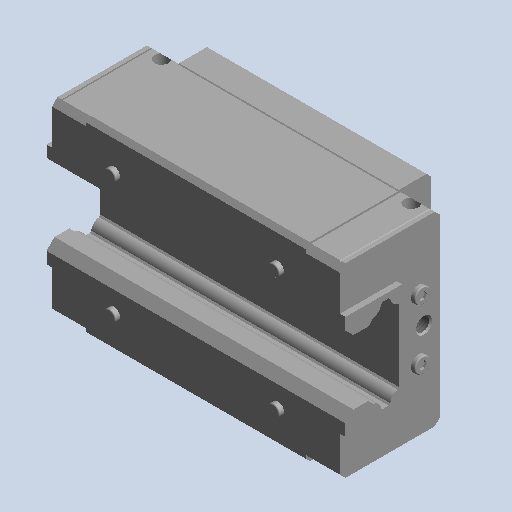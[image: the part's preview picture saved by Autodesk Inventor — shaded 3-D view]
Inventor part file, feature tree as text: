
AUTODESK INVENTOR PART (.ipt)
format: ipt  version: 2022 (Build 260153000, 153)  size: 424,960 bytes
history: native  units: mm (DEFAULTED — no unit token found)
features: sketch x39, extrude x22, other x21, revolve x10, hole x7, pattern_linear x1
ambient origin geometry x8: Origin, YZ Plane, XZ Plane, XY Plane, X Axis, Y Axis, Z Axis, Center Point
bodies: Solid1 (feature_tree)
feature tree (100):
  extrude  "Extrusion1"  Depth=2.0mm
  hole  "Hole1"  [1 undecoded]
  pattern_linear  "Rectangular Pattern1"  [2 undecoded]
  extrude  "Extrusion2"  [1 undecoded]
  extrude  "Extrusion3"  [1 undecoded]
  extrude  "Extrusion4"  [1 undecoded]
  extrude  "Extrusion5"  [1 undecoded]
  extrude  "Extrusion6"  [1 undecoded]
  extrude  "Extrusion7"  [1 undecoded]
  hole  "Hole2"  [1 undecoded]
  hole  "Hole3"  [1 undecoded]
  extrude  "Extrusion8"  [1 undecoded]
  extrude  "Extrusion9"  [1 undecoded]
  extrude  "Extrusion10"  [1 undecoded]
  extrude  "Extrusion11"  [1 undecoded]
  extrude  "Extrusion12"  [1 undecoded]
  revolve  "Revolution1"  [1 undecoded]
  revolve  "Revolution2"  [1 undecoded]
  revolve  "Revolution3"  [1 undecoded]
  revolve  "Revolution4"  [1 undecoded]
  extrude  "Extrusion13"  [1 undecoded]
  extrude  "Extrusion14"  [1 undecoded]
  extrude  "Extrusion15"  [1 undecoded]
  extrude  "Extrusion16"  [1 undecoded]
  extrude  "Extrusion17"  [1 undecoded]
  extrude  "Extrusion18"  [1 undecoded]
  extrude  "Extrusion19"  [1 undecoded]
  extrude  "Extrusion20"  [1 undecoded]
  extrude  "Extrusion21"  [1 undecoded]
  extrude  "Extrusion22"  [1 undecoded]
  hole  "Hole4"  [1 undecoded]
  hole  "Hole5"  [1 undecoded]
  revolve  "Revolution5"  [1 undecoded]
  revolve  "Revolution6"  [1 undecoded]
  revolve  "Revolution7"  [1 undecoded]
  revolve  "Revolution8"  [1 undecoded]
  revolve  "Revolution9"  [1 undecoded]
  hole  "Hole6"  [1 undecoded]
  revolve  "Revolution10"  [1 undecoded]
  hole  "Hole7"  [1 undecoded]
  other  "4TRACK_XY"
  other  "4TRACK_YZ"
  other  "4TRACK_ZX"
  other  "4TRACK_X"
  other  "4TRACK_Y"
  other  "4TRACK_Z"
  other  "4TRACK_Center"
  other  "niple_XY"
  other  "niple_YZ"
  other  "niple_ZX"
  other  "niple_X"
  other  "niple_Y"
  other  "niple_Z"
  other  "niple_Center"
  other  "niple2_XY"
  other  "niple2_YZ"
  other  "niple2_ZX"
  other  "niple2_X"
  other  "niple2_Y"
  other  "niple2_Z"
  other  "niple2_Center"
  sketch  "Sketch_22"  dims[d53=360.0deg]
  sketch  "Sketch2"  dims[d2=6.647mm d3=12.6765mm d4=8.0mm d5=2.0mm d6=90.0deg d7=14.4mm d8=120.0deg d9=20.0mm d11=50.0mm d12=20.0mm d14=50.0mm]
  sketch  "Sketch_7"  dims[d23=10.5mm d24=0.0mm]
  sketch  "Sketch_2"  dims[d15=11.0mm d16=0.0mm d17=3.5mm d18=0.0mm]
  sketch  "Sketch_8"  dims[d25=10.5mm d26=0.0mm]
  sketch  "Sketch_42"  dims[d82=4.917mm d83=5.5415mm d84=6.0mm d85=2.0mm d86=90.0deg d87=6.0mm d88=120.0deg]
  sketch  "Sketch_106"  dims[d102=5.2mm d103=6.0mm d104=4.0mm d105=2.0mm d106=90.0deg d107=5.2mm d108=0.0mm]
  sketch  "Sketch_107"  dims[d109=0.0mm d110=0.0mm]
  sketch  "Sketch9"  dims[d27=6.2mm d28=6.0mm d29=4.0mm d30=2.0mm d31=90.0deg d32=1.0mm d33=0.0mm]
  sketch  "Sketch10"  dims[d34=6.2mm d35=6.0mm d36=4.0mm d37=2.0mm d38=90.0deg d39=1.0mm d40=0.0mm]
  sketch  "Sketch_1"  dims[d0=80.4mm d1=0.0mm]
  sketch  "Sketch_6"  dims[d21=3.5mm d22=0.0mm]
  sketch  "Sketch_20"  dims[d51=360.0deg]
  sketch  "Sketch_21"  dims[d52=360.0deg]
  sketch  "Sketch_65"  dims[d93=360.0deg]
  sketch  "Sketch_4"  dims[d19=11.0mm d20=0.0mm]
  sketch  "Sketch_14"  dims[d45=2.0mm d46=0.0mm]
  sketch  "Sketch_15"  dims[d47=2.0mm d48=0.0mm]
  sketch  "Sketch_16"  dims[d49=109.4mm d50=0.0mm]
  sketch  "Sketch_24"  dims[d54=360.0deg]
  sketch  "Sketch_25"  dims[d55=0.75mm d56=0.0mm]
  sketch  "Sketch_26"  dims[d57=0.75mm d58=0.0mm]
  sketch  "Sketch_27"  dims[d59=0.75mm d60=0.0mm]
  sketch  "Sketch_12"  dims[d41=2.0mm d42=0.0mm]
  sketch  "Sketch_13"  dims[d43=2.0mm d44=0.0mm]
  sketch  "Sketch_45"  dims[d89=360.0deg]
  sketch  "Sketch_46"  dims[d90=360.0deg]
  sketch  "Sketch_47"  dims[d91=360.0deg]
  sketch  "Sketch_48"  dims[d92=360.0deg]
  sketch  "Sketch30"  dims[d61=0.75mm d62=0.0mm]
  sketch  "Sketch31"  dims[d63=68.0mm d64=0.0mm]
  sketch  "Sketch_34"  dims[d65=68.0mm d66=0.0mm]
  sketch  "Sketch_35"  dims[d67=47.5mm d68=0.0mm]
  sketch  "Sketch_37"  dims[d69=47.5mm d70=0.0mm]
  sketch  "Sketch_38"  dims[d73=47.5mm d74=0.0mm]
  sketch  "Sketch_94"  dims[d94=5.2mm d95=6.0mm d96=4.0mm d97=2.0mm d98=90.0deg d99=5.2mm d100=0.0mm]
  sketch  "Sketch37"  dims[d71=47.5mm d72=0.0mm]
  sketch  "Sketch_96"  dims[d101=360.0deg]
  sketch  "Sketch39"  dims[d75=4.917mm d76=5.5415mm d77=6.0mm d78=2.0mm d79=90.0deg d80=6.0mm d81=120.0deg]
note: 40 required parameter values undecoded (feature->parameter linkage not recoverable at this tier; creation-order binding heuristic only, values carry confidence <= 0.55)
